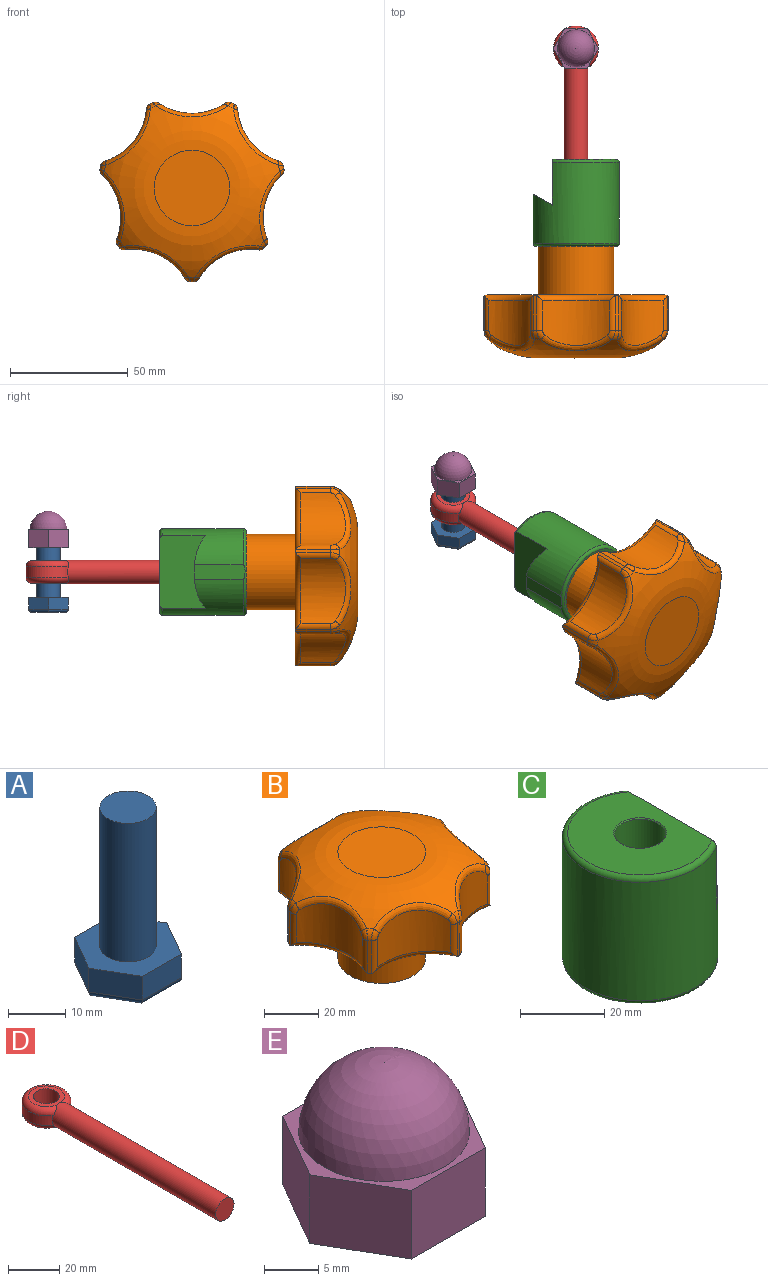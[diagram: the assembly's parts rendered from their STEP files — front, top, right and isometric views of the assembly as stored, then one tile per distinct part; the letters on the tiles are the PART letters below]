
ASSEMBLY  parts=5 mates=4
PART A: 16 faces, bbox 19.4x16.8x36 mm
  f0: plane 8.38x5.08mm, normal (0.87,-0.5,0), area 49.2mm2, adj f1,f5,f6,f10
  f1: plane 8.38x5.08mm, normal (0.87,0.5,0), area 49.2mm2, adj f0,f2,f6,f8
  f2: plane 9.68x5.08mm, normal (0,1,0), area 49.2mm2, adj f1,f3,f6,f9
  f3: plane 8.38x5.08mm, normal (-0.87,0.5,0), area 49.2mm2, adj f2,f4,f6,f11
  f4: plane 8.38x5.08mm, normal (-0.87,-0.5,0), area 49.2mm2, adj f3,f5,f6,f13
  f5: plane 9.68x5.08mm, normal (0,-1,0), area 49.2mm2, adj f0,f4,f6,f12
  f6: plane 19.36x16.76mm, normal (0,0,1), area 166.7mm2, adj f0,f1,f2,f3,f4,f5,f14
  f7: plane 16.42x14.22mm, normal (0,0,-1), area 175.2mm2, adj f8,f9,f10,f11,f12,f13
  f8: cylinder r=1.27mm len=9.02mm, axis (-0.5,0.87,0), area 18.2mm2, adj f1,f7,f9,f10
  f9: cylinder r=1.27mm len=9.68mm, axis (-1,0,0), area 18.2mm2, adj f2,f7,f8,f11
  f10: cylinder r=1.27mm len=9.02mm, axis (0.5,0.87,0), area 18.2mm2, adj f0,f7,f8,f12
  f11: cylinder r=1.27mm len=9.02mm, axis (-0.5,-0.87,0), area 18.2mm2, adj f3,f7,f9,f13
  f12: cylinder r=1.27mm len=9.68mm, axis (1,0,0), area 18.2mm2, adj f5,f7,f10,f13
  f13: cylinder r=1.27mm len=9.02mm, axis (0.5,-0.87,0), area 18.2mm2, adj f4,f7,f11,f12
  f14: cylinder r=4.94mm len=29.69mm, axis (0,0,-1), area 921.7mm2, adj f6,f15
  f15: plane 9.88x9.88mm, normal (0,0,1), area 76.7mm2, adj f14
PART B: 70 faces, bbox 80.3x78.8x47.7 mm
  f0: torus R=16.09mm, axis (0,0,1), area 2755.1mm2, adj f3,f4,f6,f9,f10,f13,f14,f20
  f1: cylinder r=39.94mm len=15.03mm, axis (0,0,1), area 21.4mm2, adj f3,f56,f64,f68,f69
  f2: cylinder r=39.94mm len=15.03mm, axis (0,0,1), area 21.3mm2, adj f4,f61,f65,f66,f68
  f3: torus R=34.86mm, axis (0,0,-1), area 9.4mm2, adj f0,f1,f46,f67
  f4: torus R=34.86mm, axis (0,0,-1), area 9.4mm2, adj f0,f2,f55,f62
  f5: cylinder r=39.94mm len=15.03mm, axis (0,0,1), area 21.4mm2, adj f6,f48,f57,f58,f64
  f6: torus R=34.86mm, axis (0,0,-1), area 9.4mm2, adj f0,f5,f37,f47
  f7: cylinder r=39.94mm len=15.03mm, axis (0,0,1), area 21.4mm2, adj f10,f40,f41,f50,f51
  f8: cylinder r=39.94mm len=15.03mm, axis (0,0,1), area 21.4mm2, adj f9,f39,f49,f50,f58
  f9: torus R=34.86mm, axis (0,0,-1), area 9.4mm2, adj f0,f8,f31,f38
  f10: torus R=34.86mm, axis (0,0,-1), area 9.4mm2, adj f0,f7,f32,f33
  f11: cylinder r=39.94mm len=15.03mm, axis (0,0,1), area 21.4mm2, adj f13,f53,f59,f60,f65
  f12: cylinder r=39.94mm len=15.03mm, axis (0,0,1), area 21.4mm2, adj f14,f42,f51,f52,f59
  f13: torus R=34.86mm, axis (0,0,-1), area 9.4mm2, adj f0,f11,f44,f54
  f14: torus R=34.86mm, axis (0,0,-1), area 9.4mm2, adj f0,f12,f34,f43
  f15: cylinder r=16.09mm len=32.18mm, axis (0,0,-1), area 2110.9mm2, adj f16,f19
  f16: plane 32.18x32.18mm, normal (0,0,-1), area 729.1mm2, adj f15,f17
  f17: cylinder r=5.18mm len=45.36mm, axis (0,0,-1), area 1476.9mm2, adj f16,f18
  f18: plane 10.36x10.36mm, normal (0,0,-1), area 84.3mm2, adj f17
  f19: plane 75.29x73.41mm, normal (0,0,-1), area 2375.1mm2, adj f15,f50,f51,f58,f59,f64,f65,f68
  f20: plane 32.18x32.18mm, normal (0,0,1), area 813.4mm2, adj f0
  f21: cylinder r=25.4mm len=28.4mm, axis (0,0,-1), area 521.8mm2, adj f45,f54,f55,f60,f61,f65
  f22: cylinder r=25.4mm len=27.69mm, axis (0,0,-1), area 521.8mm2, adj f29,f33,f34,f41,f42,f51
  f23: cylinder r=25.4mm len=25.59mm, axis (0,0,-1), area 521.8mm2, adj f30,f37,f38,f48,f49,f58
  f24: cylinder r=25.4mm len=22.2mm, axis (0,0,-1), area 521.8mm2, adj f35,f43,f44,f52,f53,f59
  f25: cylinder r=25.4mm len=25.59mm, axis (0,0,-1), area 521.8mm2, adj f28,f31,f32,f39,f40,f50
  f26: cylinder r=25.4mm len=27.69mm, axis (0,0,-1), area 521.8mm2, adj f36,f46,f47,f56,f57,f64
  f27: cylinder r=25.4mm len=22.2mm, axis (0,0,-1), area 521.8mm2, adj f62,f63,f66,f67,f68,f69
  f28: bspline ~31.13x16.06mm, area 94.8mm2, adj f0,f25,f31,f32
  f29: bspline ~33.68x11.16mm, area 94.8mm2, adj f0,f22,f33,f34
  f30: bspline ~31.12x16.06mm, area 94.8mm2, adj f0,f23,f37,f38
  f31: bspline ~5.4x2.87mm, area 9.8mm2, adj f9,f25,f28,f39
  f32: bspline ~5.4x3.69mm, area 9.8mm2, adj f10,f25,f28,f40
  f33: bspline ~5.4x3.76mm, area 9.8mm2, adj f10,f22,f29,f41
  f34: bspline ~5.4x3.34mm, area 9.8mm2, adj f14,f22,f29,f42
  f35: bspline ~27.01x21.63mm, area 94.8mm2, adj f0,f24,f43,f44
  f36: bspline ~33.68x11.16mm, area 94.8mm2, adj f0,f26,f46,f47
  f37: bspline ~5.4x3.69mm, area 9.8mm2, adj f6,f23,f30,f48
  f38: bspline ~5.4x2.87mm, area 9.8mm2, adj f9,f23,f30,f49
  f39: cylinder r=2.54mm len=14.78mm, axis (0,0,-1), area 35.6mm2, adj f8,f25,f31,f50
  f40: cylinder r=2.54mm len=14.78mm, axis (0,0,1), area 35.6mm2, adj f7,f25,f32,f50
  f41: cylinder r=2.54mm len=14.78mm, axis (0,0,-1), area 35.6mm2, adj f7,f22,f33,f51
  f42: cylinder r=2.54mm len=14.78mm, axis (0,0,1), area 35.6mm2, adj f12,f22,f34,f51
  f43: bspline ~5.4x3.01mm, area 9.8mm2, adj f14,f24,f35,f52
  f44: bspline ~5.4x3.43mm, area 9.8mm2, adj f13,f24,f35,f53
  f45: bspline ~34.55x8.36mm, area 94.8mm2, adj f0,f21,f54,f55
  f46: bspline ~5.4x3.34mm, area 9.8mm2, adj f3,f26,f36,f56
  f47: bspline ~5.4x3.76mm, area 9.8mm2, adj f6,f26,f36,f57
  f48: cylinder r=2.54mm len=14.78mm, axis (0,0,-1), area 35.6mm2, adj f5,f23,f37,f58
  f49: cylinder r=2.54mm len=14.78mm, axis (0,0,1), area 35.6mm2, adj f8,f23,f38,f58
  f50: torus R=27.94mm, axis (0,0,1), area 135.9mm2, adj f7,f8,f19,f25,f39,f40,f51,f58
  f51: torus R=27.94mm, axis (0,0,1), area 135.9mm2, adj f7,f12,f19,f22,f41,f42,f50,f59
  f52: cylinder r=2.54mm len=14.78mm, axis (0,0,-1), area 35.6mm2, adj f12,f24,f43,f59
  f53: cylinder r=2.54mm len=14.78mm, axis (0,0,1), area 35.6mm2, adj f11,f24,f44,f59
  f54: bspline ~5.4x3.64mm, area 9.8mm2, adj f13,f21,f45,f60
  f55: bspline ~5.4x3.64mm, area 9.8mm2, adj f4,f21,f45,f61
  f56: cylinder r=2.54mm len=14.78mm, axis (0,0,-1), area 35.6mm2, adj f1,f26,f46,f64
  f57: cylinder r=2.54mm len=14.78mm, axis (0,0,1), area 35.6mm2, adj f5,f26,f47,f64
  f58: torus R=27.94mm, axis (0,0,1), area 135.9mm2, adj f5,f8,f19,f23,f48,f49,f50,f64
  f59: torus R=27.94mm, axis (0,0,1), area 135.9mm2, adj f11,f12,f19,f24,f51,f52,f53,f65
  f60: cylinder r=2.54mm len=14.78mm, axis (0,0,-1), area 35.6mm2, adj f11,f21,f54,f65
  f61: cylinder r=2.54mm len=14.78mm, axis (0,0,1), area 35.6mm2, adj f2,f21,f55,f65
  f62: bspline ~5.4x3.43mm, area 9.8mm2, adj f4,f27,f63,f66
  f63: bspline ~27.01x21.63mm, area 94.8mm2, adj f0,f27,f62,f67
  f64: torus R=27.94mm, axis (0,0,1), area 135.9mm2, adj f1,f5,f19,f26,f56,f57,f58,f68
  f65: torus R=27.94mm, axis (0,0,1), area 135.9mm2, adj f2,f11,f19,f21,f59,f60,f61,f68
  f66: cylinder r=2.54mm len=14.78mm, axis (0,0,-1), area 35.6mm2, adj f2,f27,f62,f68
  f67: bspline ~5.4x3.01mm, area 9.8mm2, adj f3,f27,f63,f69
  f68: torus R=27.94mm, axis (0,0,1), area 135.9mm2, adj f1,f2,f19,f27,f64,f65,f66,f69
  f69: cylinder r=2.54mm len=14.78mm, axis (0,0,1), area 35.6mm2, adj f1,f27,f67,f68
PART C: 11 faces, bbox 39.9x39.9x36.9 mm
  f0: cylinder r=18.41mm len=36.83mm, axis (0,0,-1), area 3298.3mm2, adj f1,f2,f4,f8,f9
  f1: torus R=17.14mm, axis (0,0,1), area 221.1mm2, adj f0,f6,f9
  f2: plane 30.76x8.03mm, normal (-0.5,0,0.87), area 206mm2, adj f0,f8,f9
  f3: plane 34.29x27.27mm, normal (0,0,1), area 664.2mm2, adj f4,f7,f8
  f4: torus R=17.14mm, axis (0,0,1), area 155.5mm2, adj f0,f3,f8
  f5: cylinder r=6.01mm len=36.5mm, axis (0,0,-1), area 1379.1mm2, adj f7,f10
  f6: plane 34.29x34.29mm, normal (0,0,-1), area 805mm2, adj f1,f10
  f7: cone r=6.01mm half-angle=45deg, axis (0,0,1), area 13.9mm2, adj f3,f5
  f8: plane 30.76x19.43mm, normal (1,0,0), area 596.8mm2, adj f0,f2,f3,f4
  f9: plane 21.58x6.1mm, normal (1,0,0), area 130.6mm2, adj f0,f1,f2
  f10: torus R=6.14mm, axis (0,0,1), area 7.6mm2, adj f5,f6
PART D: 10 faces, bbox 20.7x108.9x10.2 mm
  f0: cylinder r=9.58mm len=19.15mm, axis (0,0,-1), area 230.6mm2, adj f1,f2,f7
  f1: torus R=7.04mm, axis (0,0,1), area 193.1mm2, adj f0,f5,f6,f7
  f2: torus R=7.04mm, axis (0,0,1), area 193.1mm2, adj f0,f4,f7,f9
  f3: cylinder r=5.08mm len=10.16mm, axis (0,0,-1), area 309.7mm2, adj f4,f5
  f4: plane 14.07x14.07mm, normal (0,0,1), area 74.4mm2, adj f2,f3
  f5: plane 14.07x14.07mm, normal (0,0,-1), area 74.4mm2, adj f1,f3
  f6: plane 3.09x0.24mm, normal (0,1,0), area 0.5mm2, adj f1,f7
  f7: cylinder r=5.08mm len=91.44mm, axis (0,1,0), area 2889.8mm2, adj f0,f1,f2,f6,f8,f9
  f8: plane 10.16x10.16mm, normal (0,-1,0), area 81.1mm2, adj f7
  f9: plane 3.09x0.24mm, normal (0,1,0), area 0.5mm2, adj f2,f7
PART E: 11 faces, bbox 19.4x16.8x15.6 mm
  f0: plane 8.38x7.75mm, normal (0.87,-0.5,0), area 75mm2, adj f1,f5,f6,f7
  f1: plane 8.38x7.75mm, normal (0.87,0.5,0), area 75mm2, adj f0,f2,f6,f7
  f2: plane 9.68x7.75mm, normal (0,1,0), area 75mm2, adj f1,f3,f6,f7
  f3: plane 8.38x7.75mm, normal (-0.87,0.5,0), area 75mm2, adj f2,f4,f6,f7
  f4: plane 8.38x7.75mm, normal (-0.87,-0.5,0), area 75mm2, adj f3,f5,f6,f7
  f5: plane 9.68x7.75mm, normal (0,-1,0), area 75mm2, adj f0,f4,f6,f7
  f6: plane 19.36x16.76mm, normal (0,0,1), area 48mm2, adj f0,f1,f2,f3,f4,f5,f8
  f7: plane 19.36x16.76mm, normal (0,0,-1), area 185.8mm2, adj f0,f1,f2,f3,f4,f5,f9
  f8: sphere r=7.89mm, area 390.8mm2, adj f6
  f9: cylinder r=4.28mm len=12.7mm, axis (0,0,-1), area 341.5mm2, adj f7,f10
  f10: plane 8.56x8.56mm, normal (0,0,-1), area 57.5mm2, adj f9
PLACE A t=(-42.84,6.08,19.74)mm
PLACE B rot(axis=(1,0,0),90deg) t=(-42.84,-77.89,36.88)mm
PLACE C rot(axis=(0,0.71,0.71),180deg) t=(-42.84,-78.02,36.88)mm
PLACE D t=(-42.84,6.08,36.88)mm
PLACE E t=(-42.84,6.08,47.1)mm
MATE fastened C.f5 <-> B.f15  axis (0,1,0) through (-42.84,-77.89,36.88)mm
MATE fastened E.f9 <-> A.f14  axis (0,0,-1) through (-42.84,6.08,47.1)mm
MATE fastened D.f3 <-> A.f14  axis (0,0,-1) through (-42.84,6.08,32.03)mm
MATE fastened C.f5 <-> D.f7  axis (0,1,0) through (-42.84,-41.14,36.88)mm
